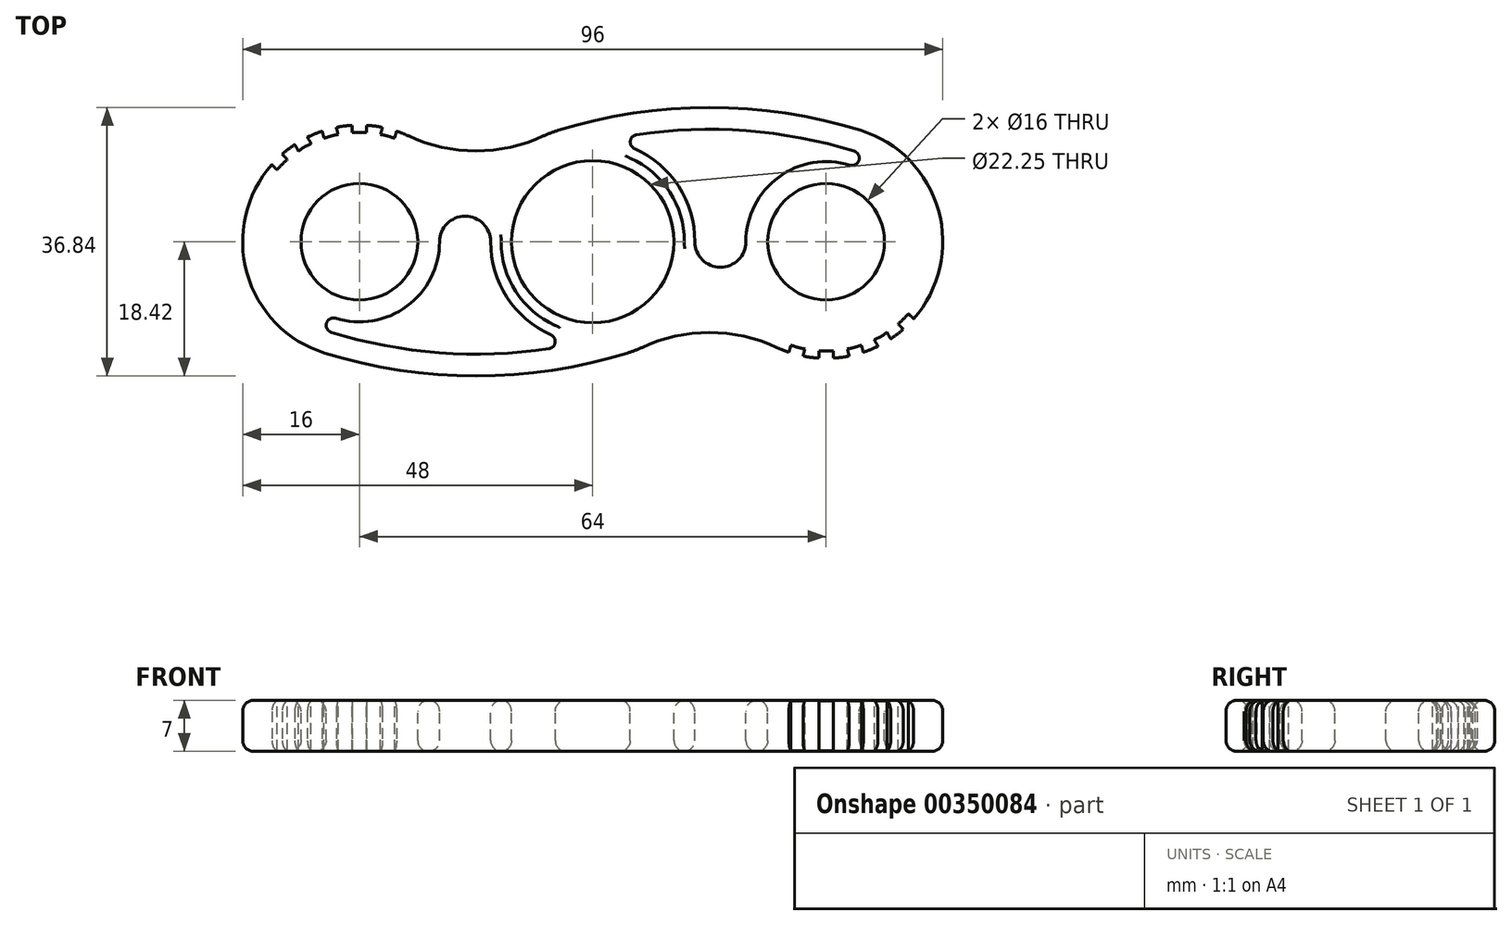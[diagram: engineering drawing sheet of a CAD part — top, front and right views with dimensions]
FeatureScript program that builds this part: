
annotation { "Feature Type Name" : "Feature", "Feature Type Description" : "" }
export const myFeature = defineFeature(function(context is Context, id is Id, definition is map)
    precondition{}
    {
        {
            var Q0;
            Q0=qCreatedBy(makeId("Top.planeOp"),FACE);
            var sketch = newSketch(context, id + "F0", { "sketchPlane" : qUnion([Q0])});
            skArc(sketch, "E0", {"start": v(4.74, -15.28) * mm, "mid": v(5.75, -14.93) * mm, "end": v(6.74, -14.51) * mm});
            skArc(sketch, "E1", {"start": v(-25.26, 14.51) * mm, "mid": v(-45.87, 7.97) * mm, "end": v(-41.14, -13.13) * mm});
            skArc(sketch, "E2", {"start": v(25.26, -14.51) * mm, "mid": v(45.87, -7.97) * mm, "end": v(41.14, 13.13) * mm});
            skArc(sketch, "E3", {"start": v(-25.26, 14.51) * mm, "mid": v(-16, 12.47) * mm, "end": v(-6.74, 14.51) * mm});
            skArc(sketch, "E4", {"start": v(25.26, -14.51) * mm, "mid": v(16, -12.47) * mm, "end": v(6.74, -14.51) * mm});
            skArc(sketch, "E5.trimOffspring", {"start": v(-4.74, 15.28) * mm, "mid": v(-5.75, 14.93) * mm, "end": v(-6.74, 14.51) * mm});
            skArc(sketch, "E6.trimOffspring", {"start": v(-41.14, -13.13) * mm, "mid": v(-39.02, -14.38) * mm, "end": v(-36.74, -15.28) * mm});
            skArc(sketch, "E7.trimOffspring", {"start": v(41.14, 13.13) * mm, "mid": v(39.02, 14.38) * mm, "end": v(36.74, 15.28) * mm});
            skArc(sketch, "E8", {"start": v(36.74, 15.28) * mm, "mid": v(16, 18.42) * mm, "end": v(-4.74, 15.28) * mm});
            skArc(sketch, "E9", {"start": v(-36.74, -15.28) * mm, "mid": v(-16, -18.42) * mm, "end": v(4.74, -15.28) * mm});
            skSolve(sketch);
        }
        {
            var Q0;
            Q0=qSketchRegion(id+"F0",true);
            extrude(context, id + "F1", {"entities" : qUnion([Q0]), "depth" : 7 * mm});
        }
        {
            var Q0;
            Q0=makeQuery(id+"F1.opExtrude","CAP_FACE",FACE,{"disambiguationData":[OSD([sQuery(id+"F0.wireOp",EDGE,"E0"),sQuery(id+"F0.wireOp",EDGE,"E1"),sQuery(id+"F0.wireOp",EDGE,"E2"),sQuery(id+"F0.wireOp",EDGE,"E3"),sQuery(id+"F0.wireOp",EDGE,"U9qsNBJu-XeLE-ORlb-NQLH-GNNNRFqsx3aL"),sQuery(id+"F0.wireOp",EDGE,"KtAAOo4r-4s1N-9Oyr-xdw8-T3c3s2v9GRLw"),sQuery(id+"F0.wireOp",EDGE,"E4"),sQuery(id+"F0.wireOp",EDGE,"E5.trimOffspring")])],"isStart":false});
            var sketch = newSketch(context, id + "F2", { "sketchPlane" : qUnion([Q0])});
            skCircle(sketch, "E10", {"center": v(0, 0) * mm, "radius": 11.12 * mm});
            skPoint(sketch, "E10.perimeterSnap0", {"position": v(-5.75, 14.93) * mm});
            skPoint(sketch, "E10.perimeterSnap1", {"position": v(-16, 12.47) * mm});
            skCircle(sketch, "E11", {"center": v(-32, 0) * mm, "radius": 8 * mm});
            skCircle(sketch, "E12", {"center": v(32, 0) * mm, "radius": 8 * mm});
            skSolve(sketch);
        }
        {
            var Q0;
            Q0=qSketchRegion(id+"F2",true);
            extrude(context, id + "F3", {"entities" : qUnion([Q0]), "operationType" : NewBodyOperationType.REMOVE, "endBound" : BoundingType.THROUGH_ALL, "oppositeDirection" : true, "depth" : 25 * mm});
        }
        {
            var Q0;
            Q0=makeQuery(id+"F1.opExtrude","CAP_FACE",FACE,{"disambiguationData":[OSD([sQuery(id+"F0.wireOp",EDGE,"E0"),sQuery(id+"F0.wireOp",EDGE,"E1"),sQuery(id+"F0.wireOp",EDGE,"E2"),sQuery(id+"F0.wireOp",EDGE,"E3"),sQuery(id+"F0.wireOp",EDGE,"E4"),sQuery(id+"F0.wireOp",EDGE,"E5.trimOffspring"),sQuery(id+"F0.wireOp",EDGE,"hpOvTq7A-kyfb-DXtC-TEhA-or5gheuMUULX"),sQuery(id+"F0.wireOp",EDGE,"wBePiWC6-iGpO-Zq4v-ABb4-8q9CdOJLcKBH"),sQuery(id+"F0.wireOp",EDGE,"ZJYLghvL-pm70-bnTZ-rQ5k-KHeNHSjt74Mt"),sQuery(id+"F0.wireOp",EDGE,"E6.trimOffspring"),sQuery(id+"F0.wireOp",EDGE,"bhJmbQDj-123R-5zu5-01mg-wOOI3Yt0Lu7z"),sQuery(id+"F0.wireOp",EDGE,"YeVEtyaY-yGgt-7S4g-LW9z-fGMiD1Vh3O3b"),sQuery(id+"F0.wireOp",EDGE,"oH4s39by-uDe5-ougK-N1i2-lCchJTmDNlGg"),sQuery(id+"F0.wireOp",EDGE,"E7.trimOffspring"),sQuery(id+"F0.wireOp",EDGE,"E8"),sQuery(id+"F0.wireOp",EDGE,"E9")])],"isStart":false});
            var sketch = newSketch(context, id + "F4", { "sketchPlane" : qUnion([Q0])});
            skArc(sketch, "E13", {"start": v(-35.85, -12.42) * mm, "mid": v(-21.05, -15.23) * mm, "end": v(-6, -14.67) * mm});
            skArc(sketch, "E14", {"start": v(-14, 0) * mm, "mid": v(-11.75, -7.6) * mm, "end": v(-5.73, -12.77) * mm});
            skArc(sketch, "E15.trimOffspring", {"start": v(-35.26, -10.5) * mm, "mid": v(-25.48, -8.86) * mm, "end": v(-21, 0) * mm});
            skArc(sketch, "E16.trimOffspring", {"start": v(14, 0) * mm, "mid": v(11.75, 7.6) * mm, "end": v(5.73, 12.77) * mm});
            skArc(sketch, "E17.trimOffspring", {"start": v(35.26, 10.5) * mm, "mid": v(25.48, 8.86) * mm, "end": v(21, 0) * mm});
            skArc(sketch, "E18.trimOffspring", {"start": v(35.85, 12.42) * mm, "mid": v(21.05, 15.23) * mm, "end": v(6, 14.67) * mm});
            skArc(sketch, "E19.filletArc", {"start": v(-35.26, -10.5) * mm, "mid": v(-36.51, -11.16) * mm, "end": v(-35.85, -12.42) * mm});
            skArc(sketch, "E20.filletArc", {"start": v(-6, -14.67) * mm, "mid": v(-5.15, -13.82) * mm, "end": v(-5.73, -12.77) * mm});
            skArc(sketch, "E21.filletArc", {"start": v(6, 14.67) * mm, "mid": v(5.15, 13.82) * mm, "end": v(5.73, 12.77) * mm});
            skArc(sketch, "E22.filletArc", {"start": v(35.26, 10.5) * mm, "mid": v(36.51, 11.16) * mm, "end": v(35.85, 12.42) * mm});
            skArc(sketch, "E23", {"start": v(-14, 0) * mm, "mid": v(-17.5, 3.5) * mm, "end": v(-21, 0) * mm});
            skArc(sketch, "E24", {"start": v(14, 0) * mm, "mid": v(17.5, -3.5) * mm, "end": v(21, 0) * mm});
            skSolve(sketch);
        }
        {
            var Q0;
            Q0 = qSketchRegion(id + "F4", true);
            extrude(context, id + "F5", {"entities" : qUnion([Q0]), "operationType" : NewBodyOperationType.REMOVE, "endBound" : BoundingType.THROUGH_ALL, "oppositeDirection" : true, "depth" : 25 * mm});
        }
        {
            var Q0;
            Q0=makeQuery(id+"F1.opExtrude","CAP_FACE",FACE,{"disambiguationData":[OSD([sQuery(id+"F0.wireOp",EDGE,"E0"),sQuery(id+"F0.wireOp",EDGE,"E1"),sQuery(id+"F0.wireOp",EDGE,"E2"),sQuery(id+"F0.wireOp",EDGE,"E3"),sQuery(id+"F0.wireOp",EDGE,"E4"),sQuery(id+"F0.wireOp",EDGE,"E5.trimOffspring"),sQuery(id+"F0.wireOp",EDGE,"hpOvTq7A-kyfb-DXtC-TEhA-or5gheuMUULX"),sQuery(id+"F0.wireOp",EDGE,"wBePiWC6-iGpO-Zq4v-ABb4-8q9CdOJLcKBH"),sQuery(id+"F0.wireOp",EDGE,"ZJYLghvL-pm70-bnTZ-rQ5k-KHeNHSjt74Mt"),sQuery(id+"F0.wireOp",EDGE,"E6.trimOffspring"),sQuery(id+"F0.wireOp",EDGE,"bhJmbQDj-123R-5zu5-01mg-wOOI3Yt0Lu7z"),sQuery(id+"F0.wireOp",EDGE,"YeVEtyaY-yGgt-7S4g-LW9z-fGMiD1Vh3O3b"),sQuery(id+"F0.wireOp",EDGE,"oH4s39by-uDe5-ougK-N1i2-lCchJTmDNlGg"),sQuery(id+"F0.wireOp",EDGE,"E7.trimOffspring"),sQuery(id+"F0.wireOp",EDGE,"E8"),sQuery(id+"F0.wireOp",EDGE,"E9")])],"isStart":false});
            var Q1;
            Q1=makeQuery(id+"F1.opExtrude","CAP_FACE",FACE,{"disambiguationData":[OSD([sQuery(id+"F0.wireOp",EDGE,"E0"),sQuery(id+"F0.wireOp",EDGE,"E1"),sQuery(id+"F0.wireOp",EDGE,"E2"),sQuery(id+"F0.wireOp",EDGE,"E3"),sQuery(id+"F0.wireOp",EDGE,"E4"),sQuery(id+"F0.wireOp",EDGE,"E5.trimOffspring"),sQuery(id+"F0.wireOp",EDGE,"hpOvTq7A-kyfb-DXtC-TEhA-or5gheuMUULX"),sQuery(id+"F0.wireOp",EDGE,"wBePiWC6-iGpO-Zq4v-ABb4-8q9CdOJLcKBH"),sQuery(id+"F0.wireOp",EDGE,"ZJYLghvL-pm70-bnTZ-rQ5k-KHeNHSjt74Mt"),sQuery(id+"F0.wireOp",EDGE,"E6.trimOffspring"),sQuery(id+"F0.wireOp",EDGE,"bhJmbQDj-123R-5zu5-01mg-wOOI3Yt0Lu7z"),sQuery(id+"F0.wireOp",EDGE,"YeVEtyaY-yGgt-7S4g-LW9z-fGMiD1Vh3O3b"),sQuery(id+"F0.wireOp",EDGE,"oH4s39by-uDe5-ougK-N1i2-lCchJTmDNlGg"),sQuery(id+"F0.wireOp",EDGE,"E7.trimOffspring"),sQuery(id+"F0.wireOp",EDGE,"E8"),sQuery(id+"F0.wireOp",EDGE,"E9")])],"isStart":true});
            fillet(context, id + "F6", {"entities" : qUnion([Q0, Q1]), "radius" : 1.5 * mm, "tangentPropagation" : true, "allowEdgeOverflow" : false});
        }
        {
            var Q0;
            Q0=makeQuery(id+"F1.opExtrude","CAP_FACE",FACE,{"disambiguationData":[OSD([sQuery(id+"F0.wireOp",EDGE,"E0"),sQuery(id+"F0.wireOp",EDGE,"E1"),sQuery(id+"F0.wireOp",EDGE,"E2"),sQuery(id+"F0.wireOp",EDGE,"E3"),sQuery(id+"F0.wireOp",EDGE,"E4"),sQuery(id+"F0.wireOp",EDGE,"E5.trimOffspring"),sQuery(id+"F0.wireOp",EDGE,"E6.trimOffspring"),sQuery(id+"F0.wireOp",EDGE,"E7.trimOffspring"),sQuery(id+"F0.wireOp",EDGE,"E8"),sQuery(id+"F0.wireOp",EDGE,"E9")])],"isStart":false});
            var sketch = newSketch(context, id + "F7", { "sketchPlane" : qUnion([Q0])});
            skArc(sketch, "E25", {"start": v(-31, 14.97) * mm, "mid": v(-32, 15) * mm, "end": v(-33, 14.97) * mm});
            skArc(sketch, "E26", {"start": v(-31, 16.97) * mm, "mid": v(-32, 17) * mm, "end": v(-33, 16.97) * mm});
            skLineSegment(sketch, "E27.0", {"start": v(-31, 14.97) * mm, "end": v(-31, 16.97) * mm});
            skLineSegment(sketch, "E28.0", {"start": v(-33, 14.97) * mm, "end": v(-33, 16.97) * mm});
            skArc(sketch, "E29.1.0", {"start": v(-34.9, 14.72) * mm, "mid": v(-35.88, 14.49) * mm, "end": v(-36.84, 14.2) * mm});
            skLineSegment(sketch, "E29.1.1", {"start": v(-34.9, 14.72) * mm, "end": v(-35.43, 16.65) * mm});
            skLineSegment(sketch, "E29.1.2", {"start": v(-36.84, 14.2) * mm, "end": v(-37.36, 16.13) * mm});
            skArc(sketch, "E29.1.3", {"start": v(-35.43, 16.65) * mm, "mid": v(-36.4, 16.42) * mm, "end": v(-37.36, 16.13) * mm});
            skArc(sketch, "E29.2.0", {"start": v(-38.62, 13.46) * mm, "mid": v(-39.5, 13) * mm, "end": v(-40.35, 12.46) * mm});
            skLineSegment(sketch, "E29.2.1", {"start": v(-38.62, 13.46) * mm, "end": v(-39.62, 15.2) * mm});
            skLineSegment(sketch, "E29.2.2", {"start": v(-40.35, 12.46) * mm, "end": v(-41.35, 14.2) * mm});
            skArc(sketch, "E29.2.3", {"start": v(-39.62, 15.2) * mm, "mid": v(-40.5, 14.72) * mm, "end": v(-41.35, 14.2) * mm});
            skArc(sketch, "E29.3.0", {"start": v(-41.88, 11.3) * mm, "mid": v(-42.6, 10.6) * mm, "end": v(-43.3, 9.88) * mm});
            skLineSegment(sketch, "E29.3.1", {"start": v(-41.88, 11.3) * mm, "end": v(-43.3, 12.7) * mm});
            skLineSegment(sketch, "E29.3.2", {"start": v(-43.3, 9.88) * mm, "end": v(-44.7, 11.3) * mm});
            skArc(sketch, "E29.3.3", {"start": v(-43.3, 12.7) * mm, "mid": v(-44.02, 12.02) * mm, "end": v(-44.7, 11.3) * mm});
            skArc(sketch, "E30.1.1", {"start": v(-27.16, 14.2) * mm, "mid": v(-28.12, 14.49) * mm, "end": v(-29.1, 14.72) * mm});
            skLineSegment(sketch, "E30.1.2", {"start": v(-29.1, 14.72) * mm, "end": v(-28.57, 16.65) * mm});
            skLineSegment(sketch, "E30.1.3", {"start": v(-27.16, 14.2) * mm, "end": v(-26.64, 16.13) * mm});
            skArc(sketch, "E30.1.4", {"start": v(-26.64, 16.13) * mm, "mid": v(-27.6, 16.42) * mm, "end": v(-28.57, 16.65) * mm});
            skLineSegment(sketch, "E31.MirrorCS", {"start": v(31, -14.97) * mm, "end": v(31, -16.97) * mm});
            skArc(sketch, "E32.MirrorCS", {"start": v(38.62, -13.46) * mm, "mid": v(39.5, -13) * mm, "end": v(40.35, -12.46) * mm});
            skLineSegment(sketch, "E33.MirrorCS", {"start": v(41.88, -11.3) * mm, "end": v(43.3, -12.7) * mm});
            skArc(sketch, "E34.MirrorCS", {"start": v(34.9, -14.72) * mm, "mid": v(35.88, -14.49) * mm, "end": v(36.84, -14.2) * mm});
            skLineSegment(sketch, "E35.MirrorCS", {"start": v(29.1, -14.72) * mm, "end": v(28.57, -16.65) * mm});
            skLineSegment(sketch, "E36.MirrorCS", {"start": v(27.16, -14.2) * mm, "end": v(26.64, -16.13) * mm});
            skArc(sketch, "E37.MirrorCS", {"start": v(41.88, -11.3) * mm, "mid": v(42.6, -10.6) * mm, "end": v(43.3, -9.88) * mm});
            skArc(sketch, "E38.MirrorCS", {"start": v(31, -14.97) * mm, "mid": v(32, -15) * mm, "end": v(33, -14.97) * mm});
            skArc(sketch, "E39.MirrorCS", {"start": v(26.64, -16.13) * mm, "mid": v(27.6, -16.42) * mm, "end": v(28.57, -16.65) * mm});
            skArc(sketch, "E40.MirrorCS", {"start": v(27.16, -14.2) * mm, "mid": v(28.12, -14.49) * mm, "end": v(29.1, -14.72) * mm});
            skLineSegment(sketch, "E41.MirrorCS", {"start": v(33, -14.97) * mm, "end": v(33, -16.97) * mm});
            skLineSegment(sketch, "E42.MirrorCS", {"start": v(34.9, -14.72) * mm, "end": v(35.43, -16.65) * mm});
            skLineSegment(sketch, "E43.MirrorCS", {"start": v(43.3, -9.88) * mm, "end": v(44.7, -11.3) * mm});
            skArc(sketch, "E44.MirrorCS", {"start": v(39.62, -15.2) * mm, "mid": v(40.5, -14.72) * mm, "end": v(41.35, -14.2) * mm});
            skArc(sketch, "E45.MirrorCS", {"start": v(35.43, -16.65) * mm, "mid": v(36.4, -16.42) * mm, "end": v(37.36, -16.13) * mm});
            skLineSegment(sketch, "E46.MirrorCS", {"start": v(40.35, -12.46) * mm, "end": v(41.35, -14.2) * mm});
            skArc(sketch, "E47.MirrorCS", {"start": v(43.3, -12.7) * mm, "mid": v(44.02, -12.02) * mm, "end": v(44.7, -11.3) * mm});
            skLineSegment(sketch, "E48.MirrorCS", {"start": v(36.84, -14.2) * mm, "end": v(37.36, -16.13) * mm});
            skLineSegment(sketch, "E49.MirrorCS", {"start": v(38.62, -13.46) * mm, "end": v(39.62, -15.2) * mm});
            skArc(sketch, "E50.MirrorCS", {"start": v(31, -16.97) * mm, "mid": v(32, -17) * mm, "end": v(33, -16.97) * mm});
            skSolve(sketch);
        }
        {
            var Q0;
            Q0=qSketchRegion(id+"F7",true);
            extrude(context, id + "F8", {"entities" : qUnion([Q0]), "operationType" : NewBodyOperationType.REMOVE, "endBound" : BoundingType.THROUGH_ALL, "oppositeDirection" : true, "depth" : 25 * mm});
        }
    });
